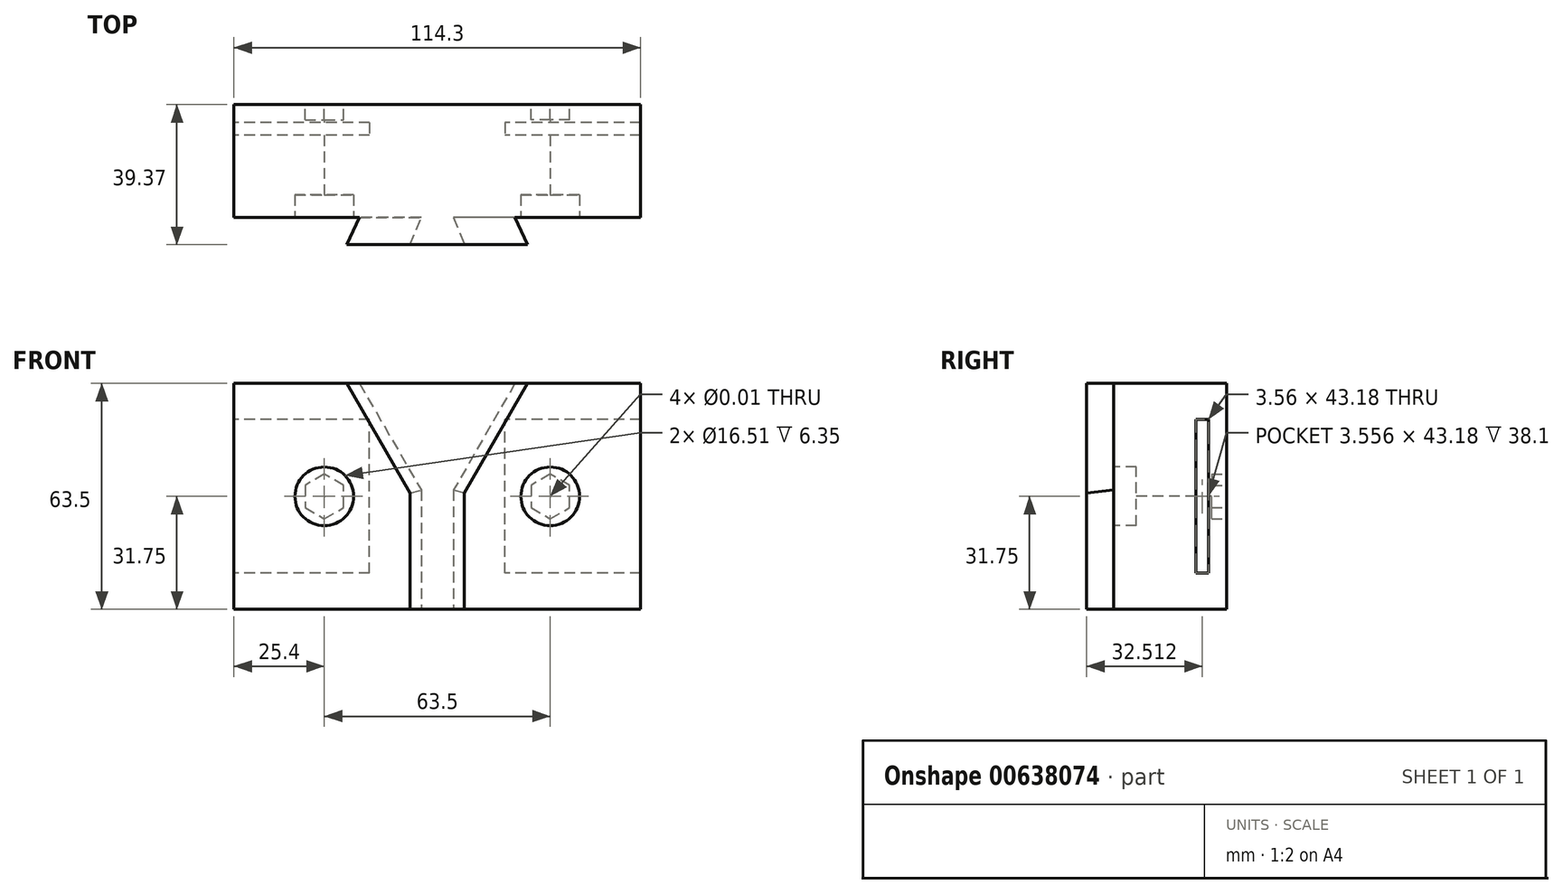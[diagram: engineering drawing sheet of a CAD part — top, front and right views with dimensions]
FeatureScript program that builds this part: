
annotation { "Feature Type Name" : "Feature", "Feature Type Description" : "" }
export const myFeature = defineFeature(function(context is Context, id is Id, definition is map)
    precondition{}
    {
        {
            var Q0;
            Q0=qCreatedBy(makeId("Right.planeOp"),FACE);
            var sketch = newSketch(context, id + "F0", { "sketchPlane" : qUnion([Q0])});
            skLineSegment(sketch, "E0", {"start": v(-26.95, -31.75) * mm, "end": v(36.55, -31.75) * mm});
            skLineSegment(sketch, "E1", {"start": v(36.55, 31.75) * mm, "end": v(-26.95, 31.75) * mm});
            skLineSegment(sketch, "E2", {"start": v(-26.95, 31.75) * mm, "end": v(-26.95, -31.75) * mm});
            skLineSegment(sketch, "E3", {"start": v(-26.95, 19.69) * mm, "end": v(-23.4, 19.69) * mm});
            skLineSegment(sketch, "E4", {"start": v(-23.4, 19.68) * mm, "end": v(-7.9, 8.89) * mm});
            skLineSegment(sketch, "E5", {"start": v(-7.9, 8.9) * mm, "end": v(-7.9, -8.9) * mm});
            skLineSegment(sketch, "E6", {"start": v(-7.9, -8.89) * mm, "end": v(-23.4, -19.68) * mm});
            skLineSegment(sketch, "E7", {"start": v(-23.4, -19.68) * mm, "end": v(-26.95, -19.68) * mm});
            skLineSegment(sketch, "E8.trimOffspring", {"start": v(36.55, -31.75) * mm, "end": v(36.55, 31.75) * mm});
            skLineSegment(sketch, "E9.trimOffspring", {"start": v(4.8, 31.75) * mm, "end": v(4.8, -31.75) * mm});
            skSolve(sketch);
        }
        {
            var Q0;
            {var subQ0=sQuery(id+"F0.wireOp",EDGE,"E8.trimOffspring");Q0=makeQuery(id+"F0.imprint","IMPRINT",FACE,{"disambiguationData":[TD([[makeQuery(id+"F0.imprint","IMPRINT",EDGE,{"derivedFrom":subQ0}),1.0]])]});}
            extrude(context, id + "F1", {"entities" : qUnion([Q0]), "depth" : 114.3 * mm, "offsetDistance" : 25.4 * mm});
        }
        {
            var Q0;
            {var subQ2=sQuery(id+"F0.wireOp",EDGE,"E3");Q0=makeQuery(id+"F0.imprint","IMPRINT",FACE,{"disambiguationData":[TD([[makeQuery(id+"F0.imprint","IMPRINT",EDGE,{"derivedFrom":subQ2}),1.0]])]});}
            var Q1;
            {var subQ0=sQuery(id+"F0.wireOp",EDGE,"E3");Q1=makeQuery(id+"F0.imprint","IMPRINT",FACE,{"disambiguationData":[TD([[makeQuery(id+"F0.imprint","IMPRINT",EDGE,{"derivedFrom":subQ0}),-1.0]])]});}
            extrude(context, id + "F2", {"entities" : qUnion([Q0, Q1]), "depth" : 114.3 * mm, "offsetDistance" : 25.4 * mm});
        }
        {
            var Q0;
            Q0=makeQuery(id+"F2.opExtrude","SWEPT_FACE",FACE,{"disambiguationData":[OSD([sQuery(id+"F0.wireOp",EDGE,"E2")])]});
            var sketch = newSketch(context, id + "F3", { "sketchPlane" : qUnion([Q0])});
            skLineSegment(sketch, "E10.0", {"start": v(0, 31.75) * mm, "end": v(0, -31.75) * mm});
            skLineSegment(sketch, "E11.0", {"start": v(25.4, 31.75) * mm, "end": v(25.4, -31.75) * mm});
            skLineSegment(sketch, "E12.0", {"start": v(-6.35, 38.1) * mm, "end": v(-6.35, -38.1) * mm});
            skLineSegment(sketch, "E12.1", {"start": v(120.65, 38.1) * mm, "end": v(-6.35, 38.1) * mm});
            skLineSegment(sketch, "E12.2", {"start": v(120.65, -38.1) * mm, "end": v(120.65, 38.1) * mm});
            skLineSegment(sketch, "E12.3", {"start": v(-6.35, -38.1) * mm, "end": v(120.65, -38.1) * mm});
            skLineSegment(sketch, "E13.0", {"start": v(88.9, 31.75) * mm, "end": v(88.9, -31.75) * mm});
            skCircle(sketch, "E14", {"center": v(25.4, 0) * mm, "radius": 4.32 * mm});
            skCircle(sketch, "E15", {"center": v(88.9, 0) * mm, "radius": 4.32 * mm});
            skSolve(sketch);
        }
        {
            var Q0;
            Q0=sQuery(id+"F3.wireOp",VERTEX,"E14.center");
            var Q1;
            Q1=sQuery(id+"F3.wireOp",VERTEX,"E15.center");
            var Q2;
            Q2=makeQuery(id+"F1.opExtrude","SWEPT_BODY",BODY,{"disambiguationData":[OSD([sQuery(id+"F0.wireOp",EDGE,"E0"),sQuery(id+"F0.wireOp",EDGE,"k3HetLsU-LdY4-jzO4-damb-BOldpCktU5Jo"),sQuery(id+"F0.wireOp",EDGE,"E1"),sQuery(id+"F0.wireOp",EDGE,"kACFFDB2-NS78-NoPQ-wamq-wGGXlr9S3aOu"),sQuery(id+"F0.wireOp",EDGE,"AuQ4PmHT-IR76-PiGX-WnEI-gpGKvU1BSqxT"),sQuery(id+"F0.wireOp",EDGE,"2K7tRHxB-wu7L-KEbF-N3xl-VGCTdnqnEJBT"),sQuery(id+"F0.wireOp",EDGE,"CM9JiyXU-7bkV-pPd9-gjAn-GurEQOhZ7tF6"),sQuery(id+"F0.wireOp",EDGE,"46d59ac6-5fc3-40f2-9007-d9fa2728f9000.MirrorCS"),sQuery(id+"F0.wireOp",EDGE,"46d59ac6-5fc3-40f2-9007-d9fa2728f9001.MirrorCS"),sQuery(id+"F0.wireOp",EDGE,"46d59ac6-5fc3-40f2-9007-d9fa2728f9002.MirrorCS"),sQuery(id+"F0.wireOp",EDGE,"E8.trimOffspring"),sQuery(id+"F0.wireOp",EDGE,"2Nn41NaE-Hgpe-s4fX-lzbf-wooGQdnGQ99G"),sQuery(id+"F0.wireOp",EDGE,"5qlYl4Ai-Fdpj-2xhL-xhdB-RVJ9mpbXSxHZ"),sQuery(id+"F0.wireOp",EDGE,"GVNRazZK-v03o-o9j3-2BiM-VDV5car0XNt5"),sQuery(id+"F0.wireOp",EDGE,"RzVRRZOU-TvBL-98Dw-26rr-Njfk6Q7A123n"),sQuery(id+"F0.wireOp",EDGE,"E9.trimOffspring")])]});
            var Q3;
            Q3=makeQuery(id+"F2.opExtrude","SWEPT_BODY",BODY,{"disambiguationData":[OSD([sQuery(id+"F0.wireOp",EDGE,"E0"),sQuery(id+"F0.wireOp",EDGE,"E1"),sQuery(id+"F0.wireOp",EDGE,"E2"),sQuery(id+"F0.wireOp",EDGE,"2Nn41NaE-Hgpe-s4fX-lzbf-wooGQdnGQ99G"),sQuery(id+"F0.wireOp",EDGE,"5qlYl4Ai-Fdpj-2xhL-xhdB-RVJ9mpbXSxHZ"),sQuery(id+"F0.wireOp",EDGE,"GVNRazZK-v03o-o9j3-2BiM-VDV5car0XNt5"),sQuery(id+"F0.wireOp",EDGE,"RzVRRZOU-TvBL-98Dw-26rr-Njfk6Q7A123n"),sQuery(id+"F0.wireOp",EDGE,"E9.trimOffspring")])]});
            hole(context, id + "F4", {"style" : HoleStyle.SIMPLE, "endStyle" : HoleEndStyle.THROUGH, "standardTappedOrClearance" : lookupTablePath({ "standard" : "ANSI", "size" : "21/64 (0.33)", "type" : "Drilled" }), "standardBlindInLast" : lookupTablePath({ "standard" : "ANSI", "size" : "21/64", "type" : "Drilled" }), "holeDiameter" : 21 / 1625.6 * mm, "majorDiameter" : 6.35 * mm, "isTappedThrough" : true, "tappedDepth" : 12.7 * mm, "tapClearance" : 3, "locations" : qUnion([Q0, Q1]), "scope" : qUnion([Q2, Q3])});
        }
        {
            var Q0;
            Q0=makeQuery(id+"F2.opExtrude","SWEPT_BODY",BODY,{"disambiguationData":[OSD([sQuery(id+"F0.wireOp",EDGE,"E0"),sQuery(id+"F0.wireOp",EDGE,"E1"),sQuery(id+"F0.wireOp",EDGE,"E2"),sQuery(id+"F0.wireOp",EDGE,"2Nn41NaE-Hgpe-s4fX-lzbf-wooGQdnGQ99G"),sQuery(id+"F0.wireOp",EDGE,"5qlYl4Ai-Fdpj-2xhL-xhdB-RVJ9mpbXSxHZ"),sQuery(id+"F0.wireOp",EDGE,"GVNRazZK-v03o-o9j3-2BiM-VDV5car0XNt5"),sQuery(id+"F0.wireOp",EDGE,"RzVRRZOU-TvBL-98Dw-26rr-Njfk6Q7A123n"),sQuery(id+"F0.wireOp",EDGE,"E9.trimOffspring")])]});
            deleteBodies(context, id + "F5", {"entities" : qUnion([Q0])});
        }
        {
            var Q0;
            Q0=makeQuery(id+"F1.opExtrude","SWEPT_FACE",FACE,{"disambiguationData":[OSD([sQuery(id+"F0.wireOp",EDGE,"E9.trimOffspring")])]});
            var sketch = newSketch(context, id + "F6", { "sketchPlane" : qUnion([Q0])});
            skLineSegment(sketch, "E16", {"start": v(57.15, 31.75) * mm, "end": v(57.15, -31.75) * mm});
            skLineSegment(sketch, "E17.0", {"start": v(31.75, 31.75) * mm, "end": v(49.53, 0.95) * mm});
            skLineSegment(sketch, "E18.0", {"start": v(-6.35, 38.1) * mm, "end": v(-6.35, -38.1) * mm});
            skLineSegment(sketch, "E18.1", {"start": v(120.65, 38.1) * mm, "end": v(-6.35, 38.1) * mm});
            skLineSegment(sketch, "E18.2", {"start": v(120.65, -38.1) * mm, "end": v(120.65, 38.1) * mm});
            skLineSegment(sketch, "E18.3", {"start": v(-6.35, -38.1) * mm, "end": v(120.65, -38.1) * mm});
            skLineSegment(sketch, "E19.0", {"start": v(82.55, 31.75) * mm, "end": v(64.77, 0.95) * mm});
            skLineSegment(sketch, "E20.0", {"start": v(49.53, 0.95) * mm, "end": v(49.53, -31.75) * mm});
            skLineSegment(sketch, "E21.0", {"start": v(64.77, 0.95) * mm, "end": v(64.77, -31.75) * mm});
            skPoint(sketch, "E22.orphan", {"position": v(50.8, -23.24) * mm});
            skSolve(sketch);
        }
        {
            var Q0;
            {var subQ2=sQuery(id+"F6.wireOp",EDGE,"E16");Q0=makeQuery(id+"F6.imprint","IMPRINT",FACE,{"disambiguationData":[TD([[makeQuery(id+"F6.imprint","IMPRINT",EDGE,{"derivedFrom":subQ2}),-1.0]])]});}
            var Q1;
            {var subQ0=sQuery(id+"F6.wireOp",EDGE,"E16");Q1=makeQuery(id+"F6.imprint","IMPRINT",FACE,{"disambiguationData":[TD([[makeQuery(id+"F6.imprint","IMPRINT",EDGE,{"derivedFrom":subQ0}),1.0]])]});}
            extrude(context, id + "F7", {"entities" : qUnion([Q0, Q1]), "operationType" : NewBodyOperationType.ADD, "depth" : 7.62 * mm, "offsetDistance" : 25.4 * mm});
        }
        {
            var Q0;
            {var subQ0=sQuery(id+"F0.wireOp",EDGE,"E8.trimOffspring");Q0=makeQuery(id+"F0.imprint","IMPRINT",FACE,{"disambiguationData":[TD([[makeQuery(id+"F0.imprint","IMPRINT",EDGE,{"derivedFrom":subQ0}),1.0]])]});}
            var sketch = newSketch(context, id + "F8", { "sketchPlane" : qUnion([Q0])});
            skLineSegment(sketch, "E23.0", {"start": v(36.55, -31.75) * mm, "end": v(36.55, 31.75) * mm});
            skLineSegment(sketch, "E24.0", {"start": v(31.47, -21.59) * mm, "end": v(31.47, 21.6) * mm});
            skLineSegment(sketch, "E25.0", {"start": v(27.91, -21.59) * mm, "end": v(27.91, 21.6) * mm});
            skPoint(sketch, "E26.orphan", {"position": v(36.55, 0) * mm});
            skLineSegment(sketch, "E27.0", {"start": v(31.47, 21.6) * mm, "end": v(27.91, 21.6) * mm});
            skLineSegment(sketch, "E28.0", {"start": v(31.47, -21.59) * mm, "end": v(27.91, -21.59) * mm});
            skSolve(sketch);
        }
        {
            var Q0;
            Q0=makeQuery(id+"F8.imprint","IMPRINT",FACE,{"disambiguationData":[TD([[makeQuery(id+"F8.imprint","IMPRINT",EDGE,{"derivedFrom":sQuery(id+"F8.wireOp",EDGE,"E24.0")}),1.0]])]});
            extrude(context, id + "F9", {"entities" : qUnion([Q0]), "operationType" : NewBodyOperationType.REMOVE, "depth" : 38.1 * mm, "offsetDistance" : 25.4 * mm});
        }
        {
            var Q0;
            Q0=makeQuery(id+"F8.imprint","IMPRINT",FACE,{"disambiguationData":[TD([[makeQuery(id+"F8.imprint","IMPRINT",EDGE,{"derivedFrom":sQuery(id+"F8.wireOp",EDGE,"E24.0")}),1.0]])]});
            extrude(context, id + "F10", {"entities" : qUnion([Q0]), "operationType" : NewBodyOperationType.REMOVE, "depth" : 114.3 * mm, "offsetDistance" : 25.4 * mm, "hasSecondDirection" : true, "secondDirectionOppositeDirection" : false, "secondDirectionDepth" : 76.2 * mm});
        }
        {
            var Q0;
            {var subQ0=sQuery(id+"F0.wireOp",EDGE,"E1");Q0=makeQuery(id+"F7.boolean.opBoolean","MERGE",FACE,{"derivedFrom":[makeQuery(id+"F1.opExtrude","SWEPT_FACE",FACE,{"disambiguationData":[OSD([subQ0])]}),makeQuery(id+"F7.opExtrude","SWEPT_FACE",FACE,{"disambiguationData":[OSD([subQ0,sQuery(id+"F0.wireOp",EDGE,"E9.trimOffspring")])]})]});}
            var sketch = newSketch(context, id + "F11", { "sketchPlane" : qUnion([Q0])});
            skLineSegment(sketch, "E29", {"start": v(31.75, 4.8) * mm, "end": v(35.3, 4.8) * mm});
            skLineSegment(sketch, "E30", {"start": v(35.3, 4.8) * mm, "end": v(31.75, -2.82) * mm});
            skLineSegment(sketch, "E31", {"start": v(82.55, 4.8) * mm, "end": v(79, 4.8) * mm});
            skLineSegment(sketch, "E32", {"start": v(79, 4.8) * mm, "end": v(82.55, -2.82) * mm});
            skSolve(sketch);
        }
        {
            var Q0;
            Q0=makeQuery(id+"F11.imprint","IMPRINT",FACE,{"disambiguationData":[TD([[makeQuery(id+"F11.imprint","IMPRINT",EDGE,{"derivedFrom":sQuery(id+"F11.wireOp",EDGE,"E29")}),-1.0]])]});
            var Q1;
            Q1=makeQuery(id+"F7.opExtrude","CAP_EDGE",EDGE,{"disambiguationData":[OSD([sQuery(id+"F6.wireOp",EDGE,"E17.0")])],"isStart":false});
            var Q2;
            Q2=makeQuery(id+"F7.opExtrude","CAP_EDGE",EDGE,{"disambiguationData":[OSD([sQuery(id+"F6.wireOp",EDGE,"E20.0")])],"isStart":false});
            sweep(context, id + "F12", {"operationType" : NewBodyOperationType.REMOVE, "profiles" : qUnion([Q0]), "path" : qUnion([Q1, Q2])});
        }
        {
            var Q0;
            Q0=makeQuery(id+"F11.imprint","IMPRINT",FACE,{"disambiguationData":[TD([[makeQuery(id+"F11.imprint","IMPRINT",EDGE,{"derivedFrom":sQuery(id+"F11.wireOp",EDGE,"E31")}),1.0]])]});
            var Q1;
            Q1=makeQuery(id+"F7.opExtrude","CAP_EDGE",EDGE,{"disambiguationData":[OSD([sQuery(id+"F6.wireOp",EDGE,"E19.0")])],"isStart":false});
            var Q2;
            Q2=makeQuery(id+"F7.opExtrude","CAP_EDGE",EDGE,{"disambiguationData":[OSD([sQuery(id+"F6.wireOp",EDGE,"E21.0")])],"isStart":false});
            sweep(context, id + "F13", {"operationType" : NewBodyOperationType.REMOVE, "profiles" : qUnion([Q0]), "path" : qUnion([Q1, Q2])});
        }
        {
            var Q0;
            {var subQ0=sQuery(id+"F6.wireOp",EDGE,"E17.0");var subQ2=sQuery(id+"F0.wireOp",EDGE,"E9.trimOffspring");var subQ3=makeQuery(id+"F1.opExtrude","SWEPT_FACE",FACE,{"disambiguationData":[OSD([subQ2])]});Q0=makeQuery(id+"F12.boolean.opBoolean","MERGE",FACE,{"derivedFrom":[makeQuery(id+"F7.boolean.opBoolean","SPLIT",FACE,{"disambiguationData":[TD([makeQuery(id+"F7.opExtrude","SWEPT_FACE",FACE,{"disambiguationData":[OSD([subQ0])]})])],"derivedFrom":subQ3}),makeQuery(id+"F12.opSweep","SWEPT_FACE",FACE,{"disambiguationData":[OSD([subQ0,sQuery(id+"F11.wireOp",EDGE,"E29")])]})]});}
            var sketch = newSketch(context, id + "F14", { "sketchPlane" : qUnion([Q0])});
            skCircle(sketch, "E33", {"center": v(25.4, 0) * mm, "radius": 8.26 * mm});
            skSolve(sketch);
        }
        {
            var Q0;
            {var subQ0=sQuery(id+"F6.wireOp",EDGE,"E19.0");var subQ3=sQuery(id+"F0.wireOp",EDGE,"E9.trimOffspring");var subQ4=makeQuery(id+"F1.opExtrude","SWEPT_FACE",FACE,{"disambiguationData":[OSD([subQ3])]});Q0=makeQuery(id+"F13.boolean.opBoolean","MERGE",FACE,{"derivedFrom":[makeQuery(id+"F7.boolean.opBoolean","SPLIT",FACE,{"disambiguationData":[TD([makeQuery(id+"F7.opExtrude","SWEPT_FACE",FACE,{"disambiguationData":[OSD([subQ0])]})])],"derivedFrom":subQ4}),makeQuery(id+"F13.opSweep","SWEPT_FACE",FACE,{"disambiguationData":[OSD([subQ0,sQuery(id+"F11.wireOp",EDGE,"E31")])]})]});}
            var sketch = newSketch(context, id + "F15", { "sketchPlane" : qUnion([Q0])});
            skCircle(sketch, "E34", {"center": v(88.9, 0) * mm, "radius": 8.26 * mm});
            skSolve(sketch);
        }
        {
            var Q0;
            Q0=makeQuery(id+"F14.imprint","IMPRINT",FACE,{"disambiguationData":[TD([[makeQuery(id+"F14.imprint","IMPRINT",EDGE,{"derivedFrom":sQuery(id+"F14.wireOp",EDGE,"E33")}),1.0]])]});
            var Q1;
            Q1=makeQuery(id+"F15.imprint","IMPRINT",FACE,{"disambiguationData":[TD([[makeQuery(id+"F15.imprint","IMPRINT",EDGE,{"derivedFrom":sQuery(id+"F15.wireOp",EDGE,"E34")}),1.0]])]});
            extrude(context, id + "F16", {"entities" : qUnion([Q0, Q1]), "operationType" : NewBodyOperationType.REMOVE, "oppositeDirection" : true, "depth" : 6.35 * mm, "offsetDistance" : 25.4 * mm});
        }
        {
            var Q0;
            Q0=makeQuery(id+"F1.opExtrude","SWEPT_FACE",FACE,{"disambiguationData":[OSD([sQuery(id+"F0.wireOp",EDGE,"E8.trimOffspring")])]});
            var sketch = newSketch(context, id + "F17", { "sketchPlane" : qUnion([Q0])});
            skCircle(sketch, "E35.cCircle", {"center": v(-88.9, 0) * mm, "radius": 5.44 * mm, "construction": true});
            skLineSegment(sketch, "E35.0", {"start": v(-83.46, 3.14) * mm, "end": v(-83.46, -3.14) * mm});
            skLineSegment(sketch, "E35.1", {"start": v(-83.46, -3.14) * mm, "end": v(-88.9, -6.28) * mm});
            skLineSegment(sketch, "E35.2", {"start": v(-88.9, -6.28) * mm, "end": v(-94.34, -3.14) * mm});
            skLineSegment(sketch, "E35.3", {"start": v(-94.34, -3.14) * mm, "end": v(-94.34, 3.14) * mm});
            skLineSegment(sketch, "E35.4", {"start": v(-94.34, 3.14) * mm, "end": v(-88.9, 6.28) * mm});
            skLineSegment(sketch, "E35.5", {"start": v(-88.9, 6.28) * mm, "end": v(-83.46, 3.14) * mm});
            skPoint(sketch, "E35.0.midPoint", {"position": v(-83.46, 0) * mm});
            skCircle(sketch, "E36.cCircle", {"center": v(-25.4, 0) * mm, "radius": 5.44 * mm, "construction": true});
            skLineSegment(sketch, "E36.0", {"start": v(-30.84, -3.14) * mm, "end": v(-30.84, 3.14) * mm});
            skLineSegment(sketch, "E36.1", {"start": v(-30.84, 3.14) * mm, "end": v(-25.4, 6.28) * mm});
            skLineSegment(sketch, "E36.2", {"start": v(-25.4, 6.28) * mm, "end": v(-19.96, 3.14) * mm});
            skLineSegment(sketch, "E36.3", {"start": v(-19.96, 3.14) * mm, "end": v(-19.96, -3.14) * mm});
            skLineSegment(sketch, "E36.4", {"start": v(-19.96, -3.14) * mm, "end": v(-25.4, -6.28) * mm});
            skLineSegment(sketch, "E36.5", {"start": v(-25.4, -6.28) * mm, "end": v(-30.84, -3.14) * mm});
            skPoint(sketch, "E36.0.midPoint", {"position": v(-30.84, 0) * mm});
            skSolve(sketch);
        }
        {
            var Q0;
            Q0=makeQuery(id+"F17.imprint","IMPRINT",FACE,{"disambiguationData":[TD([[makeQuery(id+"F17.imprint","IMPRINT",EDGE,{"derivedFrom":sQuery(id+"F17.wireOp",EDGE,"E35.0")}),-1.0]])]});
            var Q1;
            Q1=makeQuery(id+"F17.imprint","IMPRINT",FACE,{"disambiguationData":[TD([[makeQuery(id+"F17.imprint","IMPRINT",EDGE,{"derivedFrom":sQuery(id+"F17.wireOp",EDGE,"E36.0")}),-1.0]])]});
            extrude(context, id + "F18", {"entities" : qUnion([Q0, Q1]), "operationType" : NewBodyOperationType.REMOVE, "oppositeDirection" : true, "depth" : 4.27 * mm, "offsetDistance" : 25.4 * mm});
        }
    });
